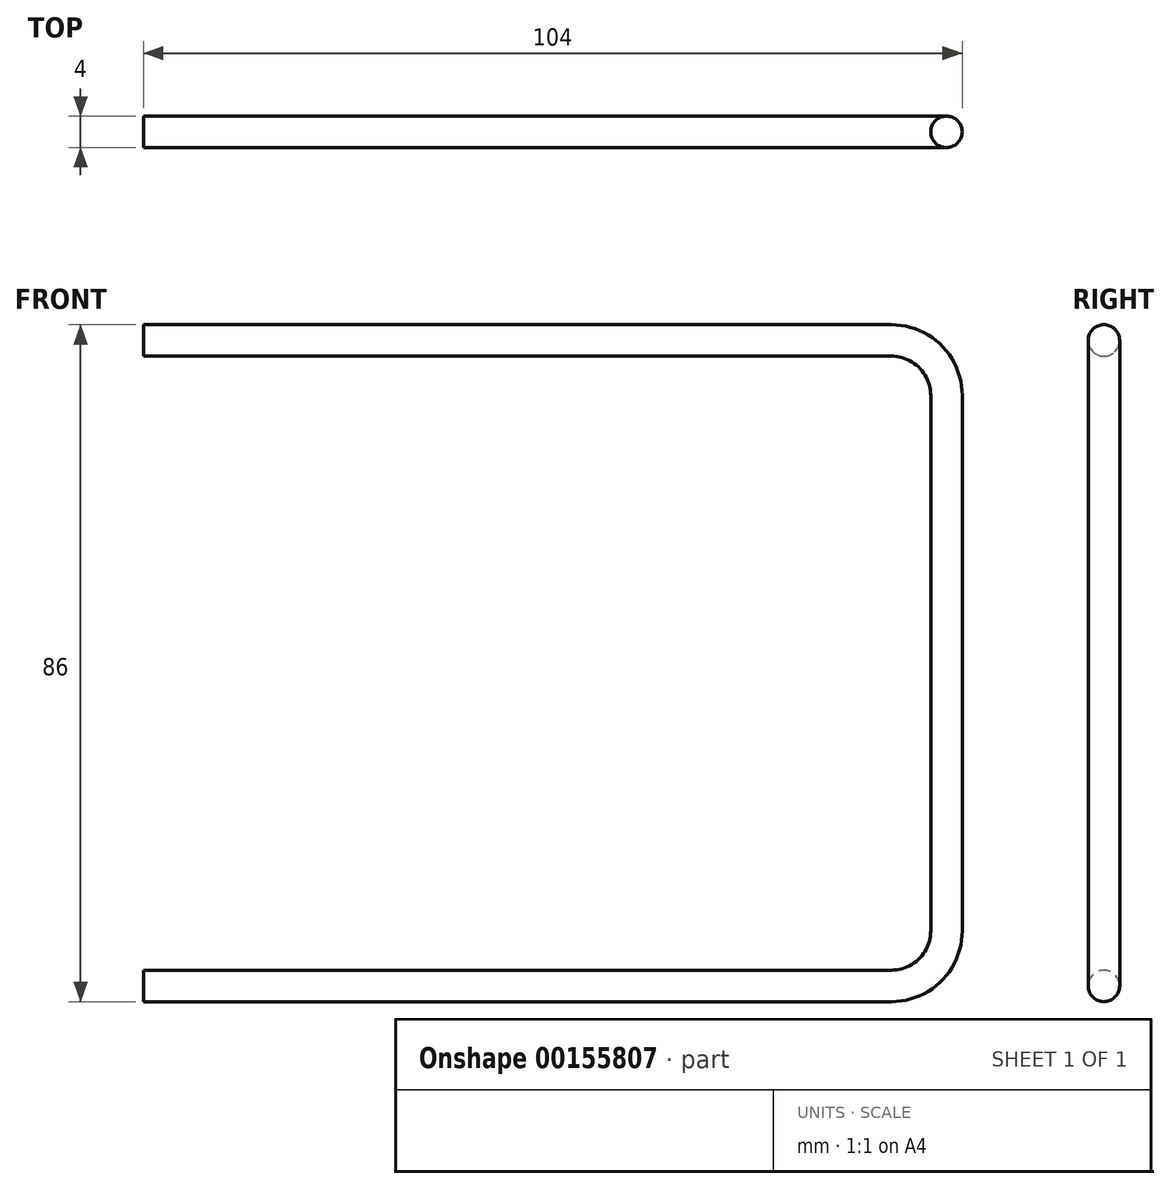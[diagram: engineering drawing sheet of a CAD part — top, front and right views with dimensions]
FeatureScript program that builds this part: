
annotation { "Feature Type Name" : "Feature", "Feature Type Description" : "" }
export const myFeature = defineFeature(function(context is Context, id is Id, definition is map)
    precondition{}
    {
        {
            var Q0;
            Q0=qCreatedBy(makeId("Front.planeOp"),FACE);
            var sketch = newSketch(context, id + "F0", { "sketchPlane" : qUnion([Q0])});
            skLineSegment(sketch, "E0", {"start": v(0, 0) * mm, "end": v(95, 0) * mm});
            skArc(sketch, "E1", {"start": v(95, 0) * mm, "mid": v(99.95, 2.05) * mm, "end": v(102, 7) * mm});
            skLineSegment(sketch, "E2", {"start": v(102, 7) * mm, "end": v(102, 75) * mm});
            skArc(sketch, "E3", {"start": v(102, 75) * mm, "mid": v(99.95, 79.95) * mm, "end": v(95, 82) * mm});
            skLineSegment(sketch, "E4", {"start": v(95, 82) * mm, "end": v(0, 82) * mm});
            skSolve(sketch);
        }
        {
            var Q0;
            Q0=qCreatedBy(makeId("Right.planeOp"),FACE);
            var sketch = newSketch(context, id + "F1", { "sketchPlane" : qUnion([Q0])});
            skCircle(sketch, "E5", {"center": v(0, 0) * mm, "radius": 2 * mm});
            skSolve(sketch);
        }
        {
            var Q0;
            Q0=makeQuery(id+"F1.imprint","IMPRINT",FACE,{"disambiguationData":[TD([[makeQuery(id+"F1.imprint","IMPRINT",EDGE,{"derivedFrom":sQuery(id+"F1.wireOp",EDGE,"E5")}),1.0]])]});
            var Q1;
            Q1=sQuery(id+"F0.wireOp",EDGE,"E4");
            var Q2;
            Q2=sQuery(id+"F0.wireOp",EDGE,"E0");
            var Q3;
            Q3=sQuery(id+"F0.wireOp",EDGE,"E1");
            var Q4;
            Q4=sQuery(id+"F0.wireOp",EDGE,"E2");
            var Q5;
            Q5=sQuery(id+"F0.wireOp",EDGE,"E3");
            sweep(context, id + "F2", {"profiles" : qUnion([Q0]), "path" : qUnion([Q1, Q2, Q3, Q4, Q5])});
        }
    });
